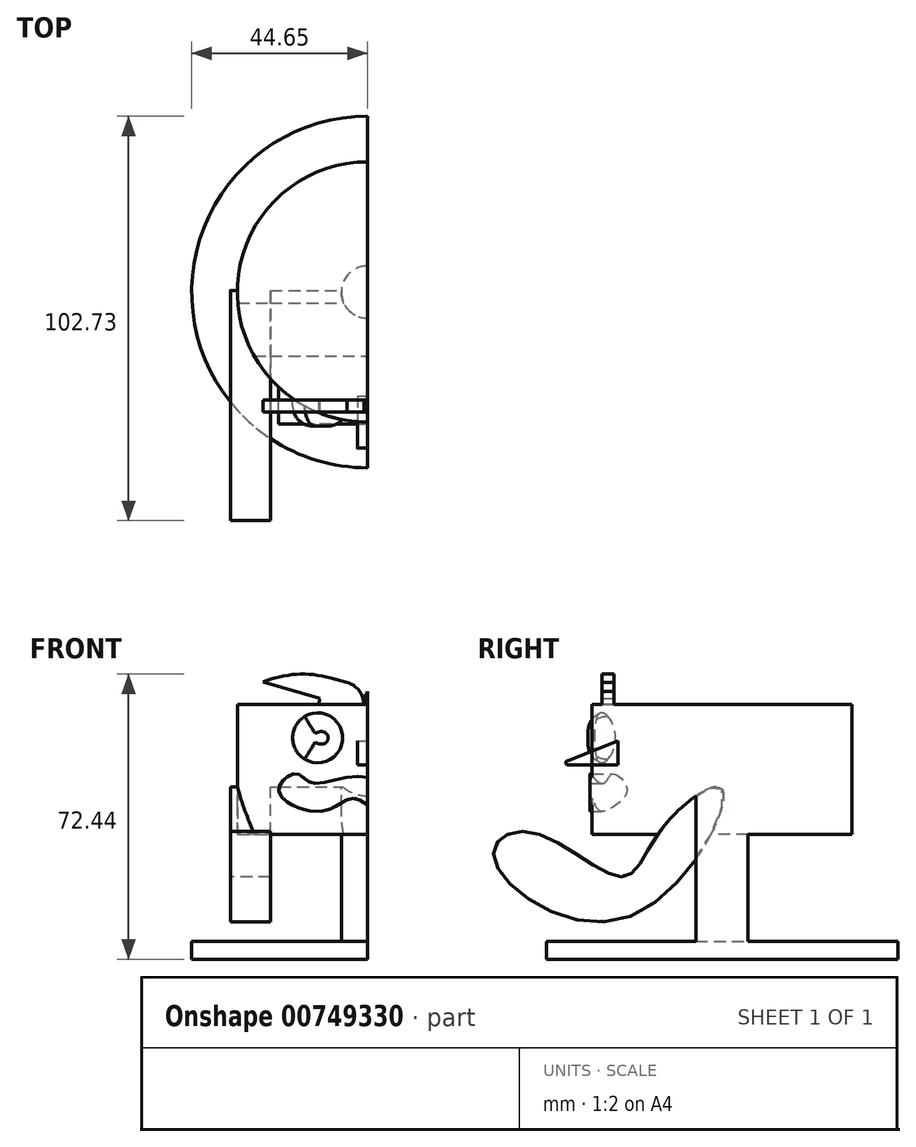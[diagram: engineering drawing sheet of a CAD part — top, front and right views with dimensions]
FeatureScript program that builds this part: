
annotation { "Feature Type Name" : "Feature", "Feature Type Description" : "" }
export const myFeature = defineFeature(function(context is Context, id is Id, definition is map)
    precondition{}
    {
        {
            var Q0;
            Q0=qCreatedBy(makeId("Top.planeOp"),FACE);
            var sketch = newSketch(context, id + "F0", { "sketchPlane" : qUnion([Q0])});
            skCircle(sketch, "E0", {"center": v(0, 0) * mm, "radius": 33.06 * mm});
            skSolve(sketch);
        }
        {
            var Q0;
            Q0 = qSketchRegion(id + "F0", true);
            extrude(context, id + "F1", {"entities" : qUnion([Q0]), "oppositeDirection" : true, "depth" : 33.02 * mm, "offsetDistance" : 25.4 * mm});
        }
        {
            var Q0;
            Q0=qCreatedBy(makeId("Front.planeOp"),FACE);
            var sketch = newSketch(context, id + "F2", { "sketchPlane" : qUnion([Q0])});
            skLineSegment(sketch, "E1", {"start": v(0, -8.52) * mm, "end": v(12.77, -8.52) * mm});
            skLineSegment(sketch, "E2", {"start": v(12.77, -8.52) * mm, "end": v(-12.63, -8.52) * mm});
            skCircle(sketch, "E3", {"center": v(-12.63, -8.52) * mm, "radius": 6.35 * mm});
            skCircle(sketch, "E4", {"center": v(12.77, -8.52) * mm, "radius": 6.35 * mm});
            skSolve(sketch);
        }
        {
            var Q0;
            Q0 = qSketchRegion(id + "F2", true);
            extrude(context, id + "F3", {"entities" : qUnion([Q0]), "operationType" : NewBodyOperationType.ADD, "depth" : 34.04 * mm, "offsetDistance" : 25.4 * mm});
        }
        {
            var Q0;
            Q0=makeQuery(id+"F3.opExtrude","CAP_FACE",FACE,{"disambiguationData":[OSD([sQuery(id+"F2.wireOp",EDGE,"E3")])],"isStart":false});
            var Q1;
            Q1=makeQuery(id+"F3.opExtrude","CAP_EDGE",EDGE,{"disambiguationData":[OSD([sQuery(id+"F2.wireOp",EDGE,"E4")])],"isStart":false});
            fillet(context, id + "F4", {"entities" : qUnion([Q0, Q1]), "radius" : 5.08 * mm, "tangentPropagation" : true, "allowEdgeOverflow" : false});
        }
        {
            var Q0;
            Q0=qCreatedBy(makeId("Front.planeOp"),FACE);
            var sketch = newSketch(context, id + "F5", { "sketchPlane" : qUnion([Q0])});
            skFitSpline(sketch, "E5", {"points": [v(-14.1, -20) * mm, v(0, -18.62) * mm, v(6.4, -23.94) * mm, v(16.46, -18.43) * mm, v(23.35, -25.13) * mm, v(17.05, -29.86) * mm, v(16.06, -25.13) * mm, v(7.98, -29.46) * mm, v(-3.05, -23.94) * mm, v(-11.33, -27.1) * mm, v(-22.56, -21.97) * mm, v(-18.03, -17.64) * mm, v(-14.1, -20) * mm]});
            skSolve(sketch);
        }
        {
            var Q0;
            Q0 = qSketchRegion(id + "F5", true);
            extrude(context, id + "F6", {"entities" : qUnion([Q0]), "operationType" : NewBodyOperationType.ADD, "depth" : 33.53 * mm, "offsetDistance" : 25.4 * mm});
        }
        {
            var Q0;
            Q0=qCreatedBy(makeId("Front.planeOp"),FACE);
            var sketch = newSketch(context, id + "F7", { "sketchPlane" : qUnion([Q0])});
            skLineSegment(sketch, "E6", {"start": v(-12.07, 1.54) * mm, "end": v(-26.5, 5.62) * mm});
            skLineSegment(sketch, "E7", {"start": v(-26.5, 5.62) * mm, "end": v(-24.96, 11.08) * mm});
            skLineSegment(sketch, "E8", {"start": v(-24.96, 11.08) * mm, "end": v(-5.2, 5.5) * mm});
            skArc(sketch, "E9", {"start": v(-12.07, 1.54) * mm, "mid": v(-12.28, -0.07) * mm, "end": v(-12.03, -1.67) * mm});
            skLineSegment(sketch, "E10", {"start": v(12.32, 1.05) * mm, "end": v(26.9, 6.6) * mm});
            skLineSegment(sketch, "E11", {"start": v(26.9, 6.6) * mm, "end": v(24.22, 13.63) * mm});
            skLineSegment(sketch, "E12", {"start": v(24.22, 13.63) * mm, "end": v(5.79, 6.62) * mm});
            skArc(sketch, "E13", {"start": v(5.79, 6.62) * mm, "mid": v(0.43, 3.88) * mm, "end": v(-0.5, -2.08) * mm});
            skPoint(sketch, "E14.orphan", {"position": v(9.56, 0) * mm});
            skLineSegment(sketch, "E15", {"start": v(-12.03, -1.67) * mm, "end": v(-1.31, -2.08) * mm});
            skLineSegment(sketch, "E16", {"start": v(-0.5, -2.08) * mm, "end": v(12.07, -2.08) * mm});
            skArc(sketch, "E17.trimOffspring", {"start": v(-1.31, -2.08) * mm, "mid": v(-1.54, 2.6) * mm, "end": v(-5.2, 5.5) * mm});
            skArc(sketch, "E18.trimOffspring", {"start": v(12.07, -2.08) * mm, "mid": v(12.38, -0.53) * mm, "end": v(12.32, 1.05) * mm});
            skSolve(sketch);
        }
        {
            var Q0;
            Q0=makeQuery(id+"F7.imprint","IMPRINT",FACE,{"disambiguationData":[TD([[makeQuery(id+"F7.imprint","IMPRINT",EDGE,{"derivedFrom":sQuery(id+"F7.wireOp",EDGE,"E6")}),-1.0]])]});
            var Q1;
            Q1=makeQuery(id+"F7.imprint","IMPRINT",FACE,{"disambiguationData":[TD([[makeQuery(id+"F7.imprint","IMPRINT",EDGE,{"derivedFrom":sQuery(id+"F7.wireOp",EDGE,"E10")}),1.0]])]});
            extrude(context, id + "F8", {"entities" : qUnion([Q0, Q1]), "operationType" : NewBodyOperationType.ADD, "depth" : 30.48 * mm, "offsetDistance" : 25.4 * mm});
        }
        {
            var Q0;
            Q0=qCreatedBy(makeId("Front.planeOp"),FACE);
            var sketch = newSketch(context, id + "F9", { "sketchPlane" : qUnion([Q0])});
            skLineSegment(sketch, "E19.bottom", {"start": v(27.8, 0) * mm, "end": v(-30.57, 0) * mm});
            skLineSegment(sketch, "E19.left", {"start": v(27.8, 0) * mm, "end": v(27.8, 11.73) * mm});
            skLineSegment(sketch, "E19.right", {"start": v(-30.57, 0) * mm, "end": v(-30.57, 11.73) * mm});
            skLineSegment(sketch, "E20.top", {"start": v(27.8, 21.68) * mm, "end": v(-30.57, 21.68) * mm});
            skLineSegment(sketch, "E20.left", {"start": v(27.8, 11.73) * mm, "end": v(27.8, 21.68) * mm});
            skLineSegment(sketch, "E20.right", {"start": v(-30.57, 11.73) * mm, "end": v(-30.57, 21.68) * mm});
            skSolve(sketch);
        }
        {
            var Q0;
            Q0=makeQuery(id+"F9.imprint","IMPRINT",FACE,{"disambiguationData":[TD([[makeQuery(id+"F9.imprint","IMPRINT",EDGE,{"derivedFrom":sQuery(id+"F9.wireOp",EDGE,"E19.bottom")}),-1.0]])]});
            extrude(context, id + "F10", {"entities" : qUnion([Q0]), "operationType" : NewBodyOperationType.REMOVE, "depth" : 27.43 * mm, "offsetDistance" : 25.4 * mm});
        }
        {
            var Q0;
            Q0=makeQuery(id+"F8.opExtrude","SWEPT_EDGE",EDGE,{"disambiguationData":[OSD([sQuery(id+"F7.wireOp",EDGE,"E7"),sQuery(id+"F7.wireOp",EDGE,"E8")])]});
            var Q1;
            Q1=makeQuery(id+"F8.opExtrude","SWEPT_EDGE",EDGE,{"disambiguationData":[OSD([sQuery(id+"F7.wireOp",EDGE,"E11"),sQuery(id+"F7.wireOp",EDGE,"E12")])]});
            fillet(context, id + "F11", {"entities" : qUnion([Q0, Q1]), "radius" : 25.75 * mm, "tangentPropagation" : true, "allowEdgeOverflow" : false});
        }
        {
            var Q0;
            Q0=qCreatedBy(makeId("Right.planeOp"),FACE);
            var sketch = newSketch(context, id + "F12", { "sketchPlane" : qUnion([Q0])});
            skLineSegment(sketch, "E21.top", {"start": v(-26.4, -15.45) * mm, "end": v(-42.16, -15.45) * mm});
            skLineSegment(sketch, "E21.left", {"start": v(-26.4, -9.34) * mm, "end": v(-26.4, -15.45) * mm});
            skLineSegment(sketch, "E22", {"start": v(-26.4, -9.34) * mm, "end": v(-42.16, -15.45) * mm});
            skSolve(sketch);
        }
        {
            var Q0;
            Q0=makeQuery(id+"F12.imprint","IMPRINT",FACE,{"disambiguationData":[TD([[makeQuery(id+"F12.imprint","IMPRINT",EDGE,{"derivedFrom":sQuery(id+"F12.wireOp",EDGE,"E21.top")}),-1.0]])]});
            extrude(context, id + "F13", {"entities" : qUnion([Q0]), "depth" : 2.54 * mm, "offsetDistance" : 25.4 * mm});
        }
        {
            var Q0;
            Q0 = qSketchRegion(id + "F12", true);
            extrude(context, id + "F14", {"entities" : qUnion([Q0]), "oppositeDirection" : true, "depth" : 2.54 * mm, "offsetDistance" : 25.4 * mm});
        }
        {
            var Q0;
            Q0=makeQuery(id+"F14.opExtrude","SWEPT_EDGE",EDGE,{"disambiguationData":[OSD([sQuery(id+"F12.wireOp",EDGE,"E21.top"),sQuery(id+"F12.wireOp",EDGE,"E22")])]});
            var Q1;
            Q1=makeQuery(id+"F13.opExtrude","SWEPT_EDGE",EDGE,{"disambiguationData":[OSD([sQuery(id+"F12.wireOp",EDGE,"E21.top"),sQuery(id+"F12.wireOp",EDGE,"E22")])]});
            fillet(context, id + "F15", {"entities" : qUnion([Q0, Q1]), "radius" : 0.57 * mm, "tangentPropagation" : true, "allowEdgeOverflow" : false});
        }
        {
            var Q0;
            Q0=qCreatedBy(makeId("Right.planeOp"),FACE);
            var sketch = newSketch(context, id + "F16", { "sketchPlane" : qUnion([Q0])});
            skFitSpline(sketch, "E23", {"points": [v(0, -15.94) * mm, v(-15.52, -30.23) * mm, v(-26.54, -42.42) * mm, v(-54.66, -41.01) * mm, v(-60.28, -47.1) * mm, v(-34.74, -53.2) * mm, v(-8.96, -44.3) * mm, v(0, -15.94) * mm]});
            skSolve(sketch);
        }
        {
            var Q0;
            Q0=makeQuery(id+"F16.imprint","IMPRINT",FACE,{"disambiguationData":[TD([[makeQuery(id+"F16.imprint","IMPRINT",EDGE,{"derivedFrom":sQuery(id+"F16.wireOp",EDGE,"E23")}),1.0]])]});
            extrude(context, id + "F17", {"entities" : qUnion([Q0]), "operationType" : NewBodyOperationType.ADD, "depth" : 33.27 * mm, "offsetDistance" : 25.4 * mm});
        }
        {
            var Q0;
            Q0 = qSketchRegion(id + "F16", true);
            extrude(context, id + "F18", {"entities" : qUnion([Q0]), "operationType" : NewBodyOperationType.REMOVE, "depth" : 24.64 * mm, "offsetDistance" : 25.4 * mm});
        }
        {
            var Q0;
            Q0=qCreatedBy(makeId("Right.planeOp"),FACE);
            var sketch = newSketch(context, id + "F19", { "sketchPlane" : qUnion([Q0])});
            skFitSpline(sketch, "E24", {"points": [v(0, -21.58) * mm, v(-15.27, -31.63) * mm, v(-25.52, -43.85) * mm, v(-48.77, -32.42) * mm, v(-58.04, -38.72) * mm, v(-24.54, -54.3) * mm, v(0, -21.58) * mm]});
            skSolve(sketch);
        }
        {
            var Q0;
            Q0=makeQuery(id+"F19.imprint","IMPRINT",FACE,{"disambiguationData":[TD([[makeQuery(id+"F19.imprint","IMPRINT",EDGE,{"derivedFrom":sQuery(id+"F19.wireOp",EDGE,"E24")}),1.0]])]});
            extrude(context, id + "F20", {"entities" : qUnion([Q0]), "operationType" : NewBodyOperationType.ADD, "oppositeDirection" : true, "depth" : 34.8 * mm, "offsetDistance" : 25.4 * mm});
        }
        {
            var Q0;
            Q0 = qSketchRegion(id + "F19", true);
            extrude(context, id + "F21", {"entities" : qUnion([Q0]), "operationType" : NewBodyOperationType.REMOVE, "oppositeDirection" : true, "depth" : 24.64 * mm, "offsetDistance" : 25.4 * mm});
        }
        {
            var Q0;
            Q0=qCreatedBy(makeId("Top.planeOp"),FACE);
            var sketch = newSketch(context, id + "F22", { "sketchPlane" : qUnion([Q0])});
            skCircle(sketch, "E25", {"center": v(0, 0) * mm, "radius": 6.64 * mm});
            skSolve(sketch);
        }
        {
            var Q0;
            Q0=makeQuery(id+"F22.imprint","IMPRINT",FACE,{"disambiguationData":[TD([[makeQuery(id+"F22.imprint","IMPRINT",EDGE,{"derivedFrom":sQuery(id+"F22.wireOp",EDGE,"E25")}),1.0]])]});
            extrude(context, id + "F23", {"entities" : qUnion([Q0]), "operationType" : NewBodyOperationType.ADD, "oppositeDirection" : true, "depth" : 64.77 * mm, "offsetDistance" : 25.4 * mm});
        }
        {
            var Q0;
            Q0=makeQuery(id+"F23.opExtrude","CAP_FACE",FACE,{"disambiguationData":[OSD([sQuery(id+"F22.wireOp",EDGE,"E25")])],"isStart":false});
            var sketch = newSketch(context, id + "F24", { "sketchPlane" : qUnion([Q0])});
            skCircle(sketch, "E26", {"center": v(0, 0) * mm, "radius": 44.65 * mm});
            skSolve(sketch);
        }
        {
            var Q0;
            Q0 = qSketchRegion(id + "F24", true);
            extrude(context, id + "F25", {"entities" : qUnion([Q0]), "operationType" : NewBodyOperationType.ADD, "oppositeDirection" : true, "depth" : 4.57 * mm, "offsetDistance" : 25.4 * mm});
        }
        {
            var Q0;
            Q0=qCreatedBy(makeId("Right.planeOp"),FACE);
            var sketch = newSketch(context, id + "F26", { "sketchPlane" : qUnion([Q0])});
            skLineSegment(sketch, "E27.bottom", {"start": v(-61.19, 21.58) * mm, "end": v(47, 21.58) * mm});
            skLineSegment(sketch, "E27.top", {"start": v(-61.19, -72.62) * mm, "end": v(47, -72.62) * mm});
            skLineSegment(sketch, "E27.left", {"start": v(-61.19, 21.58) * mm, "end": v(-61.19, -72.62) * mm});
            skLineSegment(sketch, "E27.right", {"start": v(47, 21.58) * mm, "end": v(47, -72.62) * mm});
            skSolve(sketch);
        }
        {
            var Q0;
            Q0 = qSketchRegion(id + "F26", true);
            extrude(context, id + "F27", {"entities" : qUnion([Q0]), "operationType" : NewBodyOperationType.REMOVE, "depth" : 63 * mm, "offsetDistance" : 25.4 * mm});
        }
    });
